# Revit family: ROTADO_ПереходныеЭлементы_ПереходСПрямоугольногоНаКруглое
name_source: partatom
category: Арматура воздуховодов
units: mm (PartAtom-declared; Revit-internal decimal feet)

## family parameters
Всегда вертикально = Да
На основе рабочей плоскости = Нет
Общий = Нет
При загрузке вырезать с полостями = Нет
Размер круглого соединителя = Использовать диаметр
Тип детали = Присоединяется

## types (93) — shared parameters
ADSK_URL документации изделия = https://rotado.ru
ADSK_URL страницы изделия = https://rotado.ru
ADSK_Версия Revit = 2019
ADSK_Единица измерения = шт.
ADSK_Завод-изготовитель = ROTADO
ADSK_Количество = 1
ADSK_Масса_Текст = 0
ADSK_Материал = ROTADO_Сталь_Нержавеющая_Оцинкованная
ADSK_Наименование = Переход с прямоугольного сечения на круглое
ADSK_Размер_Высота = 300 мм
L = 300 мм
URL = https://rotado.ru
Изготовитель = ROTADO
Описание = Переход с прямоугольного сечения на круглое. В основании имеет прямоугольное сечение. Вверху – круглое. Устанавливается на вентиляционные шахты прямоугольной и квадратной формы.
Производитель_Контакты_Телефон = 88007002460
zero-valued in all types: ADSK_Масса

## per-type parameters (varying)
| type | A | ADSK_Размер_Диаметр | ADSK_Размер_Длина | ADSK_Размер_Ширина | B | D | d |
| 100х100_D100 | 100 мм | 100 мм | 100 мм | 100 мм | 100 мм | 100 мм | 98 мм |
| 150х100_D100 | 150 мм | 100 мм | 150 мм | 100 мм | 100 мм | 100 мм | 98 мм |
| 150х100_D125 | 150 мм | 125 мм | 150 мм | 100 мм | 100 мм | 125 мм | 123 мм |
| 150х100_D160 | 150 мм | 160 мм | 150 мм | 100 мм | 100 мм | 160 мм | 158 мм |
| 150х150_D100 | 150 мм | 100 мм | 150 мм | 150 мм | 150 мм | 100 мм | 98 мм |
| 150х150_D125 | 150 мм | 125 мм | 150 мм | 150 мм | 150 мм | 125 мм | 123 мм |
| 150х150_D160 | 150 мм | 160 мм | 150 мм | 150 мм | 150 мм | 160 мм | 158 мм |
| 150х150_D200 | 150 мм | 200 мм | 150 мм | 150 мм | 150 мм | 200 мм | 198 мм |
| 200х100_D100 | 200 мм | 100 мм | 200 мм | 100 мм | 100 мм | 100 мм | 98 мм |
| 200х100_D125 | 200 мм | 125 мм | 200 мм | 100 мм | 100 мм | 125 мм | 123 мм |
| 200х100_D160 | 200 мм | 160 мм | 200 мм | 100 мм | 100 мм | 160 мм | 158 мм |
| 200х100_D200 | 200 мм | 200 мм | 200 мм | 100 мм | 100 мм | 200 мм | 198 мм |
| 200х150_D100 | 200 мм | 100 мм | 200 мм | 150 мм | 150 мм | 100 мм | 98 мм |
| 200х150_D125 | 200 мм | 125 мм | 200 мм | 150 мм | 150 мм | 125 мм | 123 мм |
| 200х150_D160 | 200 мм | 160 мм | 200 мм | 150 мм | 150 мм | 160 мм | 158 мм |
| 200х150_D200 | 200 мм | 200 мм | 200 мм | 150 мм | 150 мм | 200 мм | 198 мм |
| 200х200_D100 | 200 мм | 100 мм | 200 мм | 200 мм | 200 мм | 100 мм | 98 мм |
| 200х200_D150 | 200 мм | 150 мм | 200 мм | 200 мм | 200 мм | 150 мм | 148 мм |
| 200х200_D160 | 200 мм | 160 мм | 200 мм | 200 мм | 200 мм | 160 мм | 158 мм |
| 200х200_D200 | 200 мм | 200 мм | 200 мм | 200 мм | 200 мм | 200 мм | 198 мм |
| 200х200_D250 | 200 мм | 250 мм | 200 мм | 200 мм | 200 мм | 250 мм | 248 мм |
| 200х200_D315 | 200 мм | 315 мм | 200 мм | 200 мм | 200 мм | 315 мм | 313 мм |
| 250х150_D125 | 250 мм | 125 мм | 250 мм | 150 мм | 150 мм | 125 мм | 123 мм |
| 250х150_D160 | 250 мм | 160 мм | 250 мм | 150 мм | 150 мм | 160 мм | 158 мм |
| 250х150_D200 | 250 мм | 200 мм | 250 мм | 150 мм | 150 мм | 200 мм | 198 мм |
| 250х150_D250 | 250 мм | 250 мм | 250 мм | 150 мм | 150 мм | 250 мм | 248 мм |
| 250х200_D160 | 250 мм | 160 мм | 250 мм | 200 мм | 200 мм | 160 мм | 158 мм |
| 250х200_D200 | 250 мм | 200 мм | 250 мм | 200 мм | 200 мм | 200 мм | 198 мм |
| 250х200_D250 | 250 мм | 250 мм | 250 мм | 200 мм | 200 мм | 250 мм | 248 мм |
| 250х200_D315 | 250 мм | 315 мм | 250 мм | 200 мм | 200 мм | 315 мм | 313 мм |
| 250х250_D160 | 250 мм | 160 мм | 250 мм | 250 мм | 250 мм | 160 мм | 158 мм |
| 250х250_D200 | 250 мм | 200 мм | 250 мм | 250 мм | 250 мм | 200 мм | 198 мм |
| 250х250_D250 | 250 мм | 250 мм | 250 мм | 250 мм | 250 мм | 250 мм | 248 мм |
| 250х250_D315 | 250 мм | 315 мм | 250 мм | 250 мм | 250 мм | 315 мм | 313 мм |
| 300х150_D125 | 300 мм | 125 мм | 300 мм | 150 мм | 150 мм | 125 мм | 123 мм |
| 300х150_D160 | 300 мм | 160 мм | 300 мм | 150 мм | 150 мм | 160 мм | 158 мм |
| 300х150_D200 | 300 мм | 200 мм | 300 мм | 150 мм | 150 мм | 200 мм | 198 мм |
| 300х150_D250 | 300 мм | 250 мм | 300 мм | 150 мм | 150 мм | 250 мм | 248 мм |
| 300х200_D160 | 300 мм | 160 мм | 300 мм | 200 мм | 200 мм | 160 мм | 158 мм |
| 300х200_D200 | 300 мм | 200 мм | 300 мм | 200 мм | 200 мм | 200 мм | 198 мм |
| 300х200_D315 | 300 мм | 315 мм | 300 мм | 200 мм | 200 мм | 315 мм | 313 мм |
| 300х200_D400 | 300 мм | 400 мм | 300 мм | 200 мм | 200 мм | 400 мм | 398 мм |
| 300х250_D200 | 300 мм | 200 мм | 300 мм | 250 мм | 250 мм | 200 мм | 198 мм |
| 300х250_D250 | 300 мм | 250 мм | 300 мм | 250 мм | 250 мм | 250 мм | 248 мм |
| 300х250_D315 | 300 мм | 315 мм | 300 мм | 250 мм | 250 мм | 315 мм | 313 мм |
| 400х200_D160 | 400 мм | 160 мм | 400 мм | 200 мм | 200 мм | 160 мм | 158 мм |
| 400х200_D200 | 400 мм | 200 мм | 400 мм | 200 мм | 200 мм | 200 мм | 198 мм |
| 400х200_D250 | 400 мм | 250 мм | 400 мм | 200 мм | 200 мм | 250 мм | 248 мм |
| 400х200_D315 | 400 мм | 315 мм | 400 мм | 200 мм | 200 мм | 315 мм | 313 мм |
| 400х250_D250 | 400 мм | 250 мм | 400 мм | 250 мм | 250 мм | 250 мм | 248 мм |
| 400х250_D315 | 400 мм | 315 мм | 400 мм | 250 мм | 250 мм | 315 мм | 313 мм |
| 400х250_D400 | 400 мм | 400 мм | 400 мм | 250 мм | 250 мм | 400 мм | 398 мм |
| 400х300_D200 | 400 мм | 200 мм | 400 мм | 300 мм | 300 мм | 200 мм | 198 мм |
| 400х300_D250 | 400 мм | 250 мм | 400 мм | 300 мм | 300 мм | 250 мм | 248 мм |
| 400х300_D315 | 400 мм | 315 мм | 400 мм | 300 мм | 300 мм | 315 мм | 313 мм |
| 400х300_D400 | 400 мм | 400 мм | 400 мм | 300 мм | 300 мм | 400 мм | 398 мм |
| 500х200_D200 | 500 мм | 200 мм | 500 мм | 200 мм | 200 мм | 200 мм | 198 мм |
| 500х200_D250 | 500 мм | 250 мм | 500 мм | 200 мм | 200 мм | 250 мм | 248 мм |
| 500х200_D315 | 500 мм | 315 мм | 500 мм | 200 мм | 200 мм | 315 мм | 313 мм |
| 500х200_D400 | 500 мм | 400 мм | 500 мм | 200 мм | 200 мм | 400 мм | 398 мм |
| 500х250_D400 | 500 мм | 400 мм | 500 мм | 250 мм | 250 мм | 400 мм | 398 мм |
| 500х250_D250 | 500 мм | 250 мм | 500 мм | 250 мм | 250 мм | 250 мм | 248 мм |
| 500х250_D315 | 500 мм | 315 мм | 500 мм | 250 мм | 250 мм | 315 мм | 313 мм |
| 500х300_D200 | 500 мм | 200 мм | 500 мм | 300 мм | 300 мм | 200 мм | 198 мм |
| 500х300_D250 | 500 мм | 250 мм | 500 мм | 300 мм | 300 мм | 250 мм | 248 мм |
| 500х300_D315 | 500 мм | 315 мм | 500 мм | 300 мм | 300 мм | 315 мм | 313 мм |
| 500х300_D400 | 500 мм | 400 мм | 500 мм | 300 мм | 300 мм | 400 мм | 398 мм |
| 600х300_D250 | 600 мм | 250 мм | 600 мм | 300 мм | 300 мм | 250 мм | 248 мм |
| 600х300_D315 | 600 мм | 315 мм | 600 мм | 300 мм | 300 мм | 315 мм | 313 мм |
| 600х300_D400 | 600 мм | 400 мм | 600 мм | 300 мм | 300 мм | 400 мм | 398 мм |
| 600х300_D450 | 600 мм | 450 мм | 600 мм | 300 мм | 300 мм | 450 мм | 448 мм |
| 600х300_D500 | 600 мм | 500 мм | 600 мм | 300 мм | 300 мм | 500 мм | 498 мм |
| 600х400_D315 | 600 мм | 315 мм | 600 мм | 400 мм | 400 мм | 315 мм | 313 мм |
| 600х400_D400 | 600 мм | 400 мм | 600 мм | 400 мм | 400 мм | 400 мм | 398 мм |
| 600х400_D500 | 600 мм | 500 мм | 600 мм | 400 мм | 400 мм | 500 мм | 498 мм |
| 700х300_D250 | 700 мм | 250 мм | 700 мм | 300 мм | 300 мм | 250 мм | 248 мм |
| 700х300_D315 | 700 мм | 315 мм | 700 мм | 300 мм | 300 мм | 315 мм | 313 мм |
| 700х300_D400 | 700 мм | 400 мм | 700 мм | 300 мм | 300 мм | 400 мм | 398 мм |
| 700х300_D500 | 700 мм | 500 мм | 700 мм | 300 мм | 300 мм | 500 мм | 498 мм |
| 700х300_D630 | 700 мм | 630 мм | 700 мм | 300 мм | 300 мм | 630 мм | 628 мм |
| 800х500_D400 | 800 мм | 400 мм | 800 мм | 500 мм | 500 мм | 400 мм | 398 мм |
| 800х500_D500 | 800 мм | 500 мм | 800 мм | 500 мм | 500 мм | 500 мм | 498 мм |
| 800х500_D630 | 800 мм | 630 мм | 800 мм | 500 мм | 500 мм | 630 мм | 628 мм |
| 800х500_D710 | 800 мм | 710 мм | 800 мм | 500 мм | 500 мм | 710 мм | 708 мм |
| 800х500_D800 | 800 мм | 800 мм | 800 мм | 500 мм | 500 мм | 800 мм | 798 мм |
| 1000х500_D400 | 1000 мм | 400 мм | 1000 мм | 500 мм | 500 мм | 400 мм | 398 мм |
| 1000х500_D500 | 1000 мм | 500 мм | 1000 мм | 500 мм | 500 мм | 500 мм | 498 мм |
| 1000х500_D630 | 1000 мм | 630 мм | 1000 мм | 500 мм | 500 мм | 630 мм | 628 мм |
| 1000х500_D710 | 1000 мм | 710 мм | 1000 мм | 500 мм | 500 мм | 710 мм | 708 мм |
| 1000х500_D800 | 1000 мм | 800 мм | 1000 мм | 500 мм | 500 мм | 800 мм | 798 мм |
| 1200х500_D500 | 1200 мм | 500 мм | 1200 мм | 500 мм | 500 мм | 500 мм | 498 мм |
| 1200х500_D630 | 1200 мм | 630 мм | 1200 мм | 500 мм | 500 мм | 630 мм | 628 мм |
| 1200х500_D710 | 1200 мм | 710 мм | 1200 мм | 500 мм | 500 мм | 710 мм | 708 мм |

note: column(s) folded — value = type name in every type: ADSK_Марка, ADSK_Обозначение
